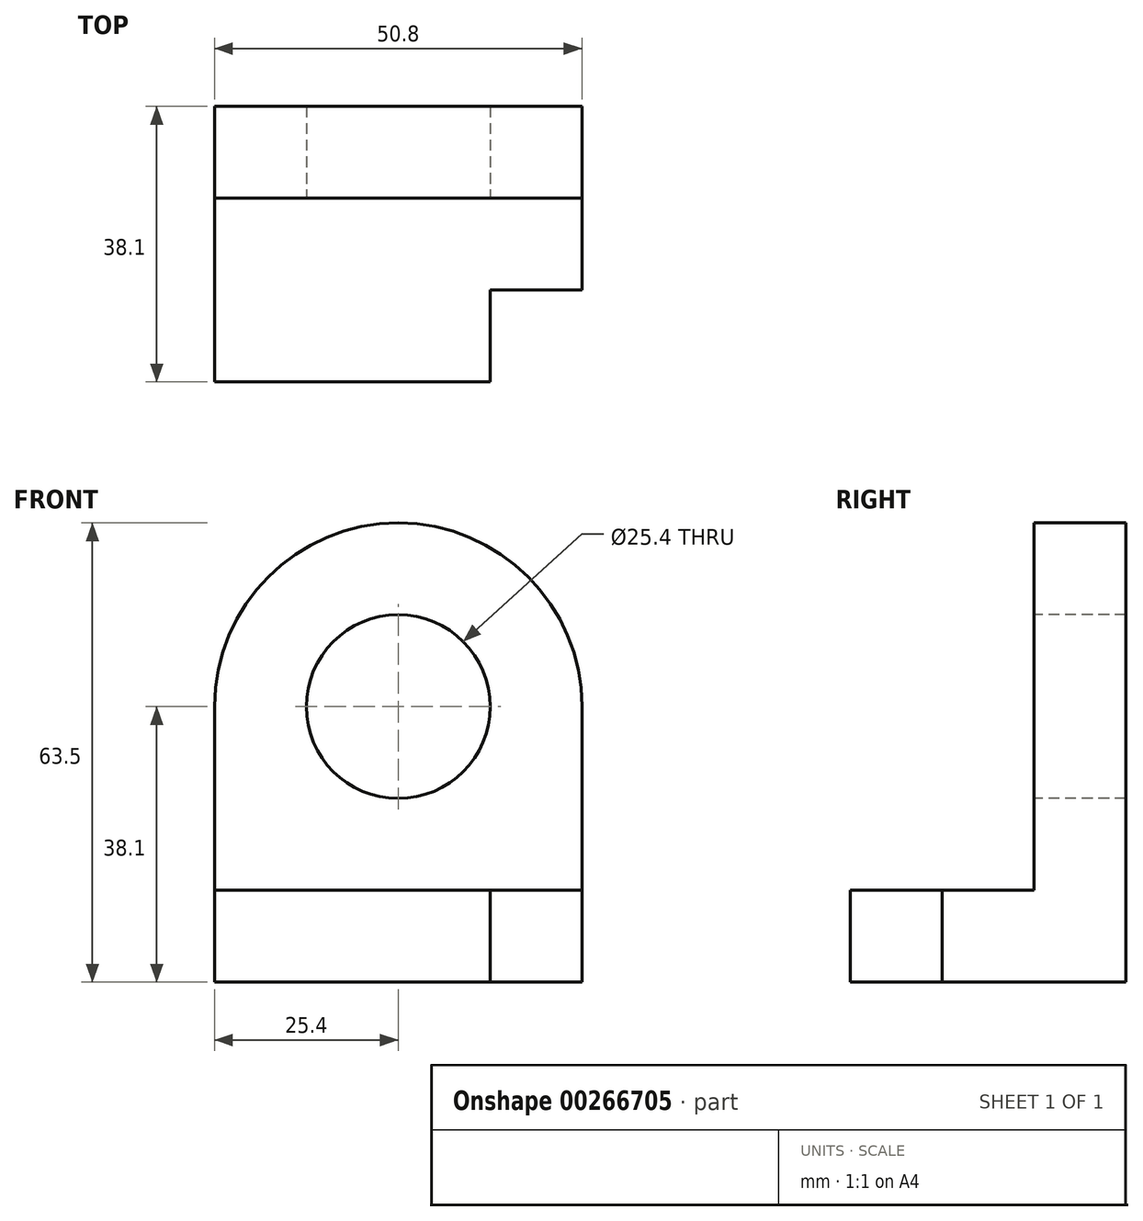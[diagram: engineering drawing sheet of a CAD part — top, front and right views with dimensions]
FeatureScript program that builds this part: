
annotation { "Feature Type Name" : "Feature", "Feature Type Description" : "" }
export const myFeature = defineFeature(function(context is Context, id is Id, definition is map)
    precondition{}
    {
        {
            var Q0;
            Q0=qCreatedBy(makeId("Top.planeOp"),FACE);
            var sketch = newSketch(context, id + "F0", { "sketchPlane" : qUnion([Q0])});
            skLineSegment(sketch, "E0.bottom", {"start": v(-25.4, 19.05) * mm, "end": v(25.4, 19.05) * mm});
            skLineSegment(sketch, "E0.top", {"start": v(-25.4, -19.05) * mm, "end": v(25.4, -19.05) * mm});
            skLineSegment(sketch, "E0.left", {"start": v(-25.4, 19.05) * mm, "end": v(-25.4, -19.05) * mm});
            skLineSegment(sketch, "E0.right", {"start": v(25.4, 19.05) * mm, "end": v(25.4, -19.05) * mm});
            skPoint(sketch, "E0.middle", {"position": v(0, 0) * mm});
            skSolve(sketch);
        }
        {
            var Q0;
            Q0=makeQuery(id+"F0.imprint","IMPRINT",FACE,{"disambiguationData":[TD([[makeQuery(id+"F0.imprint","IMPRINT",EDGE,{"derivedFrom":sQuery(id+"F0.wireOp",EDGE,"E0.bottom")}),-1.0]])]});
            extrude(context, id + "F1", {"entities" : qUnion([Q0]), "endBound" : BoundingType.SYMMETRIC, "depth" : 12.7 * mm});
        }
        {
            var Q0;
            Q0=makeQuery(id+"F1.opExtrude","CAP_FACE",FACE,{"disambiguationData":[OSD([sQuery(id+"F0.wireOp",EDGE,"E0.bottom"),sQuery(id+"F0.wireOp",EDGE,"E0.top"),sQuery(id+"F0.wireOp",EDGE,"E0.left"),sQuery(id+"F0.wireOp",EDGE,"E0.right")])],"isStart":false});
            var sketch = newSketch(context, id + "F2", { "sketchPlane" : qUnion([Q0])});
            skLineSegment(sketch, "E1.bottom", {"start": v(-25.4, 19.05) * mm, "end": v(25.4, 19.05) * mm});
            skLineSegment(sketch, "E1.top", {"start": v(-25.4, 6.35) * mm, "end": v(25.4, 6.35) * mm});
            skLineSegment(sketch, "E1.left", {"start": v(-25.4, 19.05) * mm, "end": v(-25.4, 6.35) * mm});
            skLineSegment(sketch, "E1.right", {"start": v(25.4, 19.05) * mm, "end": v(25.4, 6.35) * mm});
            skSolve(sketch);
        }
        {
            var Q0;
            Q0=makeQuery(id+"F2.imprint","IMPRINT",FACE,{"disambiguationData":[TD([[makeQuery(id+"F2.imprint","IMPRINT",EDGE,{"derivedFrom":sQuery(id+"F2.wireOp",EDGE,"E1.bottom")}),-1.0]])]});
            extrude(context, id + "F3", {"entities" : qUnion([Q0]), "operationType" : NewBodyOperationType.ADD, "depth" : 63.5 * mm});
        }
        {
            var Q0;
            Q0=makeQuery(id+"F3.opExtrude","SWEPT_FACE",FACE,{"disambiguationData":[OSD([sQuery(id+"F2.wireOp",EDGE,"E1.top")])]});
            var sketch = newSketch(context, id + "F4", { "sketchPlane" : qUnion([Q0])});
            skCircle(sketch, "E2", {"center": v(0, 31.75) * mm, "radius": 12.7 * mm});
            skSolve(sketch);
        }
        {
            var Q0;
            Q0=makeQuery(id+"F4.imprint","IMPRINT",FACE,{"disambiguationData":[TD([[makeQuery(id+"F4.imprint","IMPRINT",EDGE,{"derivedFrom":sQuery(id+"F4.wireOp",EDGE,"E2")}),1.0]])]});
            extrude(context, id + "F5", {"entities" : qUnion([Q0]), "operationType" : NewBodyOperationType.REMOVE, "oppositeDirection" : true, "depth" : 25.4 * mm});
        }
        {
            var Q0;
            Q0=makeQuery(id+"F3.opExtrude","SWEPT_FACE",FACE,{"disambiguationData":[OSD([sQuery(id+"F2.wireOp",EDGE,"E1.top")])]});
            var sketch = newSketch(context, id + "F6", { "sketchPlane" : qUnion([Q0])});
            skCircle(sketch, "E3", {"center": v(0, 31.75) * mm, "radius": 25.4 * mm});
            skSolve(sketch);
        }
        {
            var Q0;
            {var subQ1=sQuery(id+"F2.wireOp",EDGE,"E1.top");var subQ6=makeQuery(id+"F3.opExtrude","CAP_EDGE",EDGE,{"disambiguationData":[OSD([subQ1])],"isStart":false});Q0=makeQuery(id+"F6.imprint","IMPRINT",FACE,{"disambiguationData":[TD([[makeQuery(id+"F6.imprint","IMPRINT",EDGE,{"derivedFrom":subQ6}),-1.0]])]});}
            extrude(context, id + "F7", {"entities" : qUnion([Q0]), "operationType" : NewBodyOperationType.REMOVE, "oppositeDirection" : true, "depth" : 25.4 * mm});
        }
        {
            var Q0;
            Q0=makeQuery(id+"F1.opExtrude","CAP_FACE",FACE,{"disambiguationData":[OSD([sQuery(id+"F0.wireOp",EDGE,"E0.bottom"),sQuery(id+"F0.wireOp",EDGE,"E0.top"),sQuery(id+"F0.wireOp",EDGE,"E0.left"),sQuery(id+"F0.wireOp",EDGE,"E0.right")])],"isStart":false});
            var sketch = newSketch(context, id + "F8", { "sketchPlane" : qUnion([Q0])});
            skLineSegment(sketch, "E4.bottom", {"start": v(25.4, -19.05) * mm, "end": v(12.7, -19.05) * mm});
            skLineSegment(sketch, "E4.top", {"start": v(25.4, -6.35) * mm, "end": v(12.7, -6.35) * mm});
            skLineSegment(sketch, "E4.left", {"start": v(25.4, -19.05) * mm, "end": v(25.4, -6.35) * mm});
            skLineSegment(sketch, "E4.right", {"start": v(12.7, -19.05) * mm, "end": v(12.7, -6.35) * mm});
            skSolve(sketch);
        }
        {
            var Q0;
            Q0=makeQuery(id+"F8.imprint","IMPRINT",FACE,{"disambiguationData":[TD([[makeQuery(id+"F8.imprint","IMPRINT",EDGE,{"derivedFrom":sQuery(id+"F8.wireOp",EDGE,"E4.bottom")}),1.0]])]});
            extrude(context, id + "F9", {"entities" : qUnion([Q0]), "operationType" : NewBodyOperationType.REMOVE, "oppositeDirection" : true, "depth" : 25.4 * mm});
        }
    });
